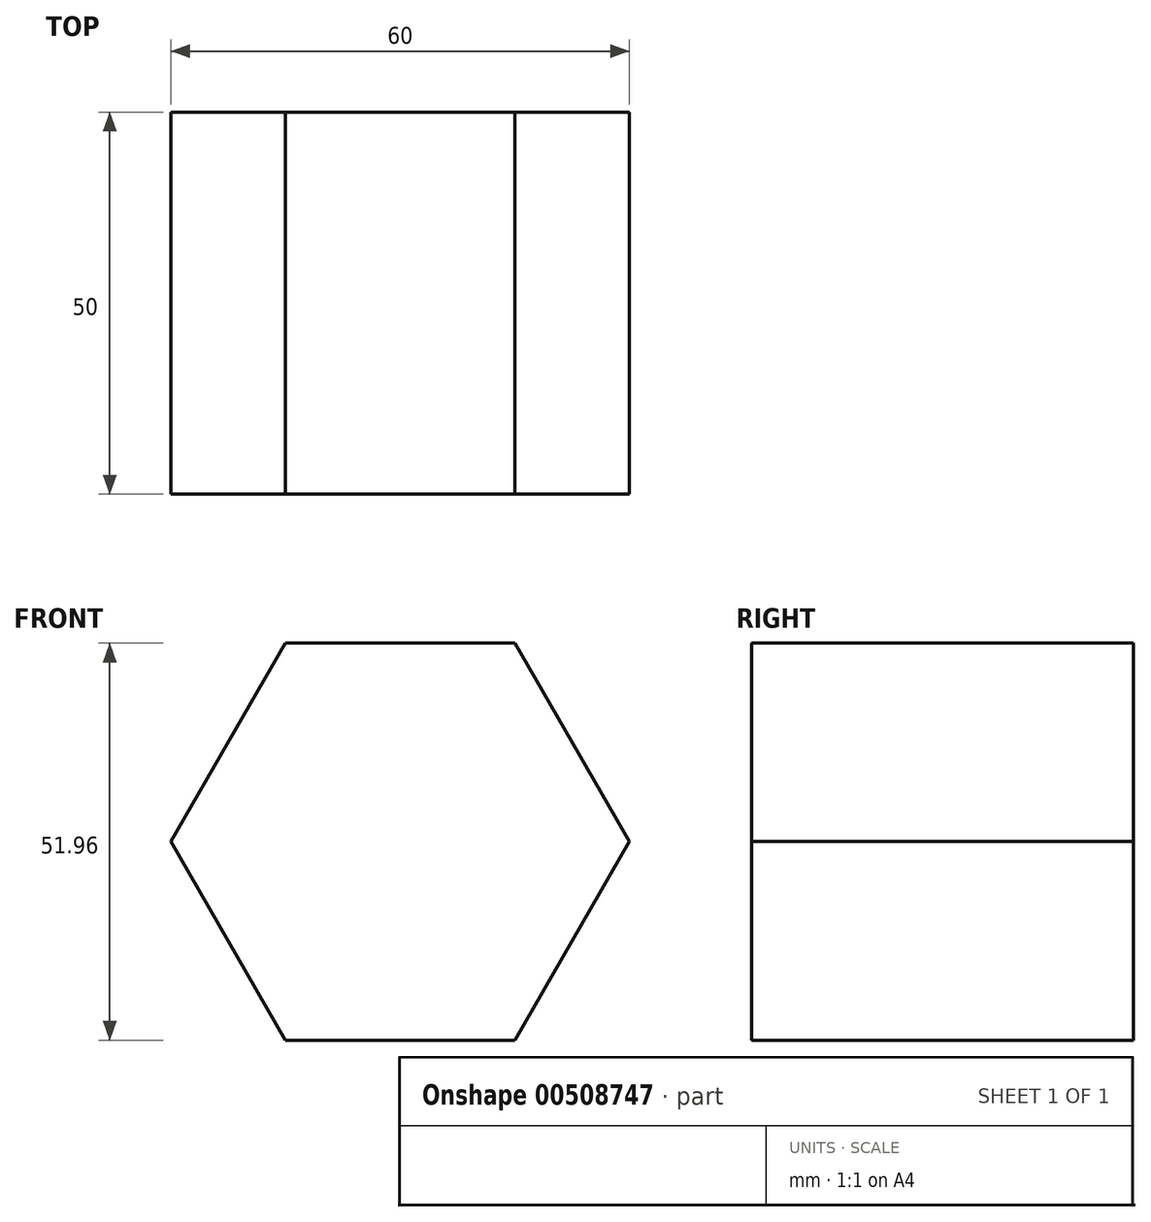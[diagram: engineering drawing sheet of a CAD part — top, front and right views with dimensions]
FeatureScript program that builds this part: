
annotation { "Feature Type Name" : "Feature", "Feature Type Description" : "" }
export const myFeature = defineFeature(function(context is Context, id is Id, definition is map)
    precondition{}
    {
        {
            var Q0;
            Q0=qCreatedBy(makeId("Front.planeOp"),FACE);
            var sketch = newSketch(context, id + "F0", { "sketchPlane" : qUnion([Q0])});
            skCircle(sketch, "E0.cCircle", {"center": v(0, 0) * mm, "radius": 30 * mm, "construction": true});
            skLineSegment(sketch, "E0.0", {"start": v(30, 0) * mm, "end": v(15, -25.98) * mm});
            skLineSegment(sketch, "E0.1", {"start": v(15, -25.98) * mm, "end": v(-15, -25.98) * mm});
            skLineSegment(sketch, "E0.2", {"start": v(-15, -25.98) * mm, "end": v(-30, 0) * mm});
            skLineSegment(sketch, "E0.3", {"start": v(-30, 0) * mm, "end": v(-15, 25.98) * mm});
            skLineSegment(sketch, "E0.4", {"start": v(-15, 25.98) * mm, "end": v(15, 25.98) * mm});
            skLineSegment(sketch, "E0.5", {"start": v(15, 25.98) * mm, "end": v(30, 0) * mm});
            skSolve(sketch);
        }
        {
            var Q0;
            Q0 = qSketchRegion(id + "F0", true);
            extrude(context, id + "F1", {"entities" : qUnion([Q0]), "depth" : 50 * mm});
        }
    });
